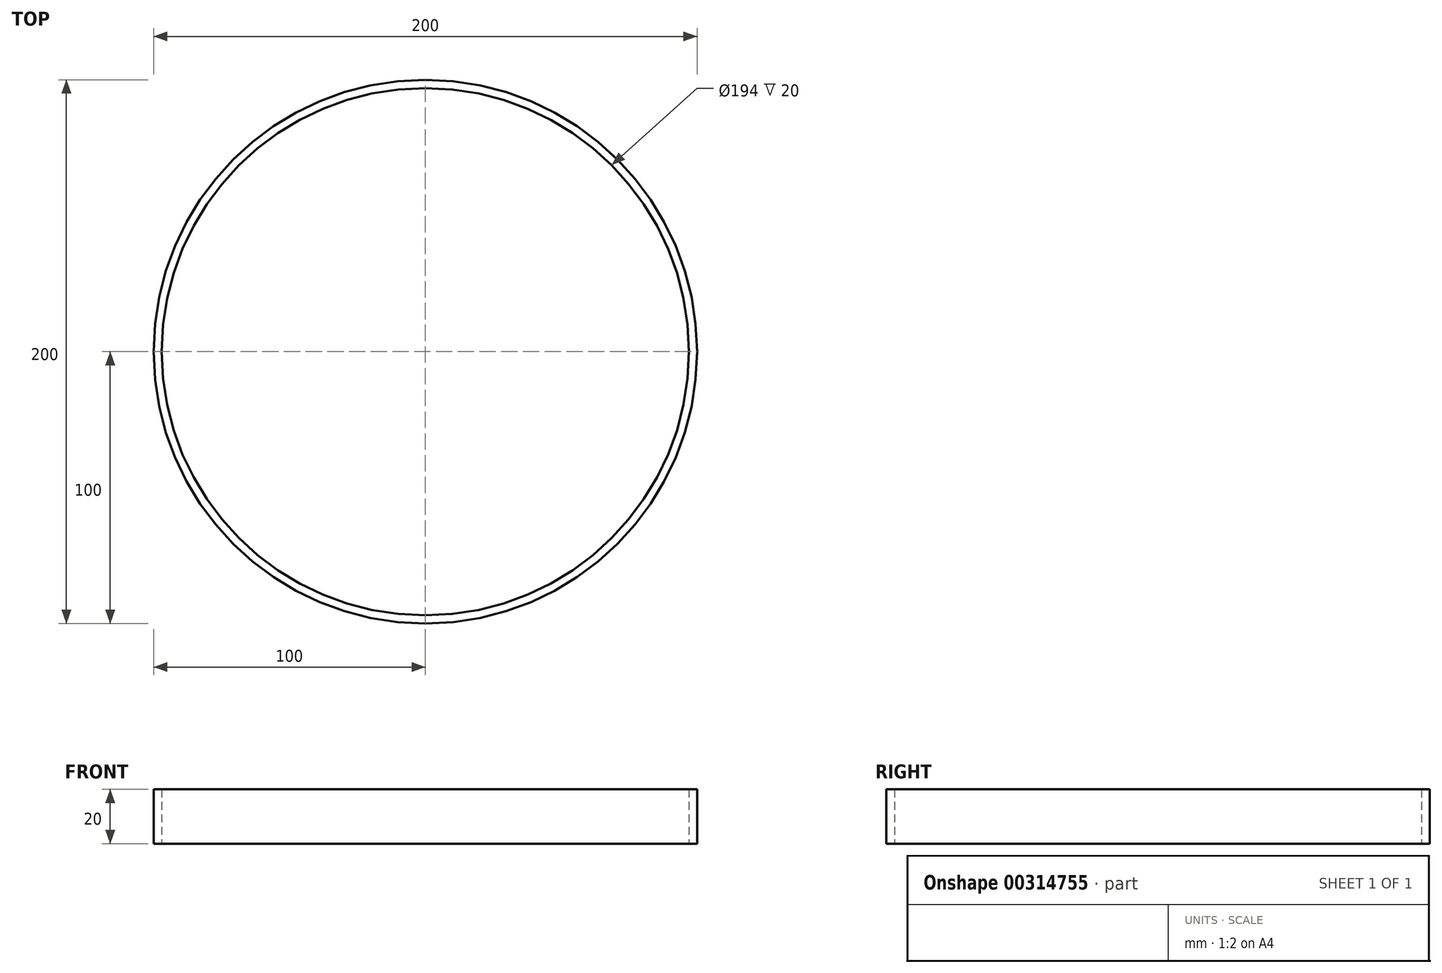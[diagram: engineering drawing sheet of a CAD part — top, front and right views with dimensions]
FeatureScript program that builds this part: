
annotation { "Feature Type Name" : "Feature", "Feature Type Description" : "" }
export const myFeature = defineFeature(function(context is Context, id is Id, definition is map)
    precondition{}
    {
        {
            var Q0;
            Q0=qCreatedBy(makeId("Top.planeOp"),FACE);
            var sketch = newSketch(context, id + "F0", { "sketchPlane" : qUnion([Q0])});
            skCircle(sketch, "E0", {"center": v(0, 0) * mm, "radius": 100 * mm});
            skCircle(sketch, "E1.0", {"center": v(0, 0) * mm, "radius": 97 * mm});
            skSolve(sketch);
        }
        {
            var Q0;
            Q0=makeQuery(id+"F0.imprint","IMPRINT",FACE,{"disambiguationData":[TD([[makeQuery(id+"F0.imprint","IMPRINT",EDGE,{"derivedFrom":sQuery(id+"F0.wireOp",EDGE,"E0")}),1.0]])]});
            extrude(context, id + "F1", {"entities" : qUnion([Q0]), "depth" : 20 * mm});
        }
    });
